# Revit family: RN 81047 Optipress-Aquaplus-Winkelverschraubung
name_source: partatom
category: Rohrformteile
units: mm (PartAtom-declared; Revit-internal decimal feet)

## family parameters
Arbeitsebenenbasiert = Nein
Beim Laden mit Abzugskörper schneiden = Nein
Bemaßung runder Anschluss = Durchmesser verwenden
Gemeinsam genutzt = Nein
Immer vertikal = Ja
Teiletyp = Verbindung

## types (9) — shared parameters
1.010.00.2 Blattnummer der Richtlinie = 29
1.010.00.3 Ausgabedatum (Monat) der Richtlinie = 201308
1.010.00.4 Herstellername = R. Nussbaum AG
1.010.00.5 Revisionsdatum der Datei = 20190521
1.010.00.6 Webadresse des Herstellers = http://www.nussbaum.ch
1.100.00.4 Produktbezeichnung = Versorgung
1.110.00.2 Index = 4
1.110.00.4 Produktbezeichnung = Optipress
1.960/3L.00.8 Link (URL) = https://www.nussbaum.ch
29.700.00.4 Produktname = Optipress-Aquaplus-Winkelverschraubung, mit Innengewinde
29.700.00.5 Produktkennung = 2
29.700.00.6 Querschnittsform = 1
29.700.00.7 Nennweitensystem = DN
29.700.00.8 Nenndrucksystem = PN
29.710.02.4 Nenndruck = 16
29.710.02.5 max. zul. Überdruck [hPa] = 1600
29.710.02.7 max. zul. Dauer-Betriebsdruck [hPa] = 1600
29.710.02.9 max. zul. Dauer-Betriebstemperatur [°C] = 95
Connector Visibility = Nein
EnclosingSpace Visibility = Nein

## per-type parameters (varying)
| type | 1.800.00.3 TGA-Nummer | 1.810.00.3 Hersteller-Bestellnummer | 1.810.00.4 DATANORM-Nummer | 1.810.00.5 StLB-Nummer | 1.810.00.6 GTIN-Nummer | 29.710.02.10 Formstück-Gewicht [kg] | 29.710.02.3 Benennung | CONNECTOR0_DIAMETER_dZ_0r | CONNECTOR0_dZ_01 | CONNECTOR0_ref_dZ | CONNECTOR1_DIAMETER_dX_0r | CONNECTOR1_dX_00 | CONNECTOR1_dX_01 | CONNECTOR1_ref_dX | CONNECTOR1_ref_dZ | R. Nussbaum AG 81047.22 de Visibility | R. Nussbaum AG 81047.23 de Visibility | R. Nussbaum AG 81047.24 de Visibility | R. Nussbaum AG 81047.25 de Visibility | R. Nussbaum AG 81047.26 de Visibility | R. Nussbaum AG 81047.29 de Visibility | R. Nussbaum AG 81047.31 de Visibility | R. Nussbaum AG 81047.33 de Visibility | R. Nussbaum AG 81047.34 de Visibility |
| 81047.22, Optipress-Aquaplus-Winkelverschraubung, mit Innengewinde, DN=12x15, L=61, Rp=½ | 01900400000000000000000000000000000000000000000029000000000000000009 | 81047.22 | 81047.22 | 266.512 | 7612945020352 | 0.185 | Optipress-Aquaplus-Winkelverschraubung, mit Innengewinde, DN=12x15, L=61, Rp=½ | 12 mm  [stored 0.0393701 ft] | 22 mm | 22 mm | 15 mm  [stored 0.0492126 ft] | 20 mm | 33 mm | 20 mm | 59 mm | Ja | Nein | Nein | Nein | Nein | Nein | Nein | Nein | Nein |
| 81047.23, Optipress-Aquaplus-Winkelverschraubung, mit Innengewinde, DN=15, L=64, Rp=½ | 01900400000000000000000000000000000000000000000029000000000000000010 | 81047.23 | 81047.23 | 266.513 | 7612945020369 | 0.18 | Optipress-Aquaplus-Winkelverschraubung, mit Innengewinde, DN=15, L=64, Rp=½ | 15 mm  [stored 0.0492126 ft] | 22 mm | 22 mm | 15 mm  [stored 0.0492126 ft] | 20 mm | 33 mm | 20 mm | 61 mm | Nein | Ja | Nein | Nein | Nein | Nein | Nein | Nein | Nein |
| 81047.24, Optipress-Aquaplus-Winkelverschraubung, mit Innengewinde, DN=15x20, L=65, Rp=¾ | 01900400000000000000000000000000000000000000000029000000000000000011 | 81047.24 | 81047.24 |  | 7612945682819 | 0.236 | Optipress-Aquaplus-Winkelverschraubung, mit Innengewinde, DN=15x20, L=65, Rp=¾ | 15 mm  [stored 0.0492126 ft] | 22 mm | 22 mm | 20 mm | 24 mm | 39 mm  [stored 0.127953 ft] | 24 mm | 65 mm | Nein | Nein | Ja | Nein | Nein | Nein | Nein | Nein | Nein |
| 81047.25, Optipress-Aquaplus-Winkelverschraubung, mit Innengewinde, DN=20, L=71, Rp=¾ | 01900400000000000000000000000000000000000000000029000000000000000012 | 81047.25 | 81047.25 | 266.514 | 7612945020376 | 0.281 | Optipress-Aquaplus-Winkelverschraubung, mit Innengewinde, DN=20, L=71, Rp=¾ | 20 mm | 24 mm | 24 mm | 20 mm | 24 mm | 39 mm  [stored 0.127953 ft] | 24 mm | 69 mm | Nein | Nein | Nein | Ja | Nein | Nein | Nein | Nein | Nein |
| 81047.26, Optipress-Aquaplus-Winkelverschraubung, mit Innengewinde, DN=20x25, L=74, Rp=1 | 01900400000000000000000000000000000000000000000029000000000000000013 | 81047.26 | 81047.26 |  | 7612945020383 | 0.442 | Optipress-Aquaplus-Winkelverschraubung, mit Innengewinde, DN=20x25, L=74, Rp=1 | 20 mm | 24 mm | 24 mm | 25 mm  [stored 0.082021 ft] | 30 mm  [stored 0.0984252 ft] | 47 mm | 30 mm  [stored 0.0984252 ft] | 75 mm | Nein | Nein | Nein | Nein | Ja | Nein | Nein | Nein | Nein |
| 81047.29, Optipress-Aquaplus-Winkelverschraubung, mit Innengewinde, DN=25, L=80, Rp=1 | 01900400000000000000000000000000000000000000000029000000000000000014 | 81047.29 | 81047.29 | 266.515 | 7612945020390 | 0.419 | Optipress-Aquaplus-Winkelverschraubung, mit Innengewinde, DN=25, L=80, Rp=1 | 25 mm  [stored 0.082021 ft] | 24 mm | 24 mm | 25 mm  [stored 0.082021 ft] | 30 mm  [stored 0.0984252 ft] | 47 mm | 30 mm  [stored 0.0984252 ft] | 80 mm | Nein | Nein | Nein | Nein | Nein | Ja | Nein | Nein | Nein |
| 81047.31, Optipress-Aquaplus-Winkelverschraubung, mit Innengewinde, DN=32, L=87, Rp=1¼ | 01900400000000000000000000000000000000000000000029000000000000000015 | 81047.31 | 81047.31 | 266.516 | 7612945020406 | 0.559 | Optipress-Aquaplus-Winkelverschraubung, mit Innengewinde, DN=32, L=87, Rp=1¼ | 32 mm | 26 mm | 26 mm | 32 mm | 38 mm | 57 mm | 38 mm | 83 mm | Nein | Nein | Nein | Nein | Nein | Nein | Ja | Nein | Nein |
| 81047.33, Optipress-Aquaplus-Winkelverschraubung, mit Innengewinde, DN=40, L=106, Rp=1½ | 01900400000000000000000000000000000000000000000029000000000000000016 | 81047.33 | 81047.33 | 266.517 | 7612945020413 | 0.854 | Optipress-Aquaplus-Winkelverschraubung, mit Innengewinde, DN=40, L=106, Rp=1½ | 40 mm | 36 mm | 36 mm | 40 mm | 40 mm | 59 mm | 40 mm | 108 mm | Nein | Nein | Nein | Nein | Nein | Nein | Nein | Ja | Nein |
| 81047.34, Optipress-Aquaplus-Winkelverschraubung, mit Innengewinde, DN=50, L=117, Rp=2 | 01900400000000000000000000000000000000000000000029000000000000000017 | 81047.34 | 81047.34 | 266.518 | 7612945020420 | 1.479 | Optipress-Aquaplus-Winkelverschraubung, mit Innengewinde, DN=50, L=117, Rp=2 | 50 mm | 40 mm | 40 mm | 50 mm | 45 mm | 69 mm | 45 mm | 111 mm | Nein | Nein | Nein | Nein | Nein | Nein | Nein | Nein | Ja |

note: column(s) folded — value = type name in every type: 1.800.00.4 Kommentarfeld

note: [stored X ft] marks values corroborated as IEEE doubles in the binary element streams (Revit-internal decimal feet)

## geometry (parser evidence)
native form markers: Sweep x3
no freeform markers — native parametric forms only
